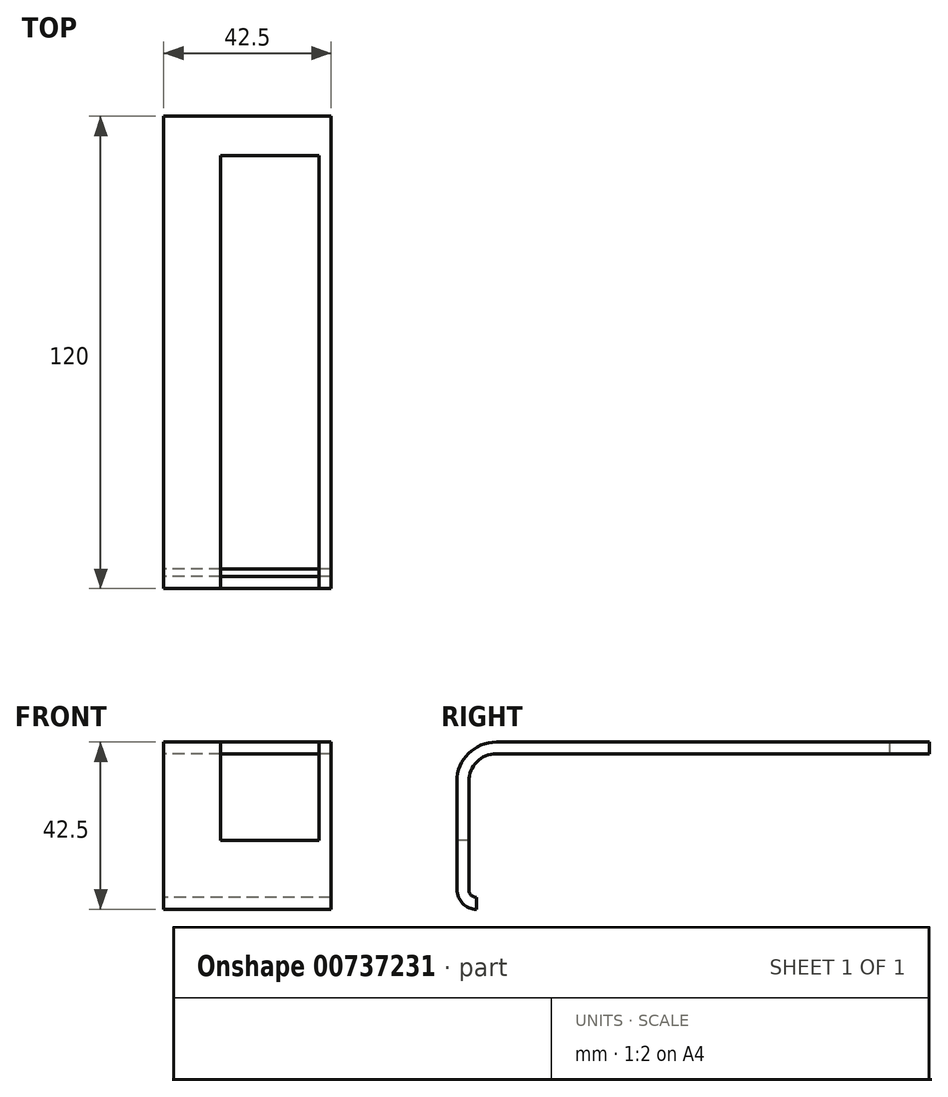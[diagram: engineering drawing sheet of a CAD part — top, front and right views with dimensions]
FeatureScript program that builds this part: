
annotation { "Feature Type Name" : "Feature", "Feature Type Description" : "" }
export const myFeature = defineFeature(function(context is Context, id is Id, definition is map)
    precondition{}
    {
        {
            var Q0;
            Q0=qCreatedBy(makeId("Right.planeOp"),FACE);
            var sketch = newSketch(context, id + "F0", { "sketchPlane" : qUnion([Q0])});
            skLineSegment(sketch, "E0", {"start": v(120, 0) * mm, "end": v(10, 0) * mm});
            skLineSegment(sketch, "E1", {"start": v(0, -10) * mm, "end": v(0, -37.5) * mm});
            skPoint(sketch, "E2.visualSharp", {"position": v(0, 0) * mm});
            skArc(sketch, "E2.filletArc", {"start": v(10, 0) * mm, "mid": v(2.93, -2.93) * mm, "end": v(0, -10) * mm});
            skPoint(sketch, "E3.visualSharp", {"position": v(0, -43) * mm});
            skArc(sketch, "E3.filletArc", {"start": v(0, -37.5) * mm, "mid": v(1.46, -41.04) * mm, "end": v(5, -42.5) * mm});
            skArc(sketch, "E4.0", {"start": v(3, -37.5) * mm, "mid": v(3.59, -38.91) * mm, "end": v(5, -39.5) * mm});
            skLineSegment(sketch, "E5.0", {"start": v(3, -10) * mm, "end": v(3, -37.5) * mm});
            skArc(sketch, "E6.0", {"start": v(10, -3) * mm, "mid": v(5.05, -5.05) * mm, "end": v(3, -10) * mm});
            skLineSegment(sketch, "E7.0", {"start": v(120, -3) * mm, "end": v(10, -3) * mm});
            skLineSegment(sketch, "E8", {"start": v(120, 0) * mm, "end": v(120, -3) * mm});
            skLineSegment(sketch, "E9", {"start": v(5, -39.5) * mm, "end": v(5, -42.5) * mm});
            skSolve(sketch);
        }
        {
            var Q0;
            Q0=qSketchRegion(id+"F0",true);
            extrude(context, id + "F1", {"entities" : qUnion([Q0]), "depth" : 42.5 * mm, "offsetDistance" : 25 * mm});
        }
        {
            var Q0;
            Q0=makeQuery(id+"F1.opExtrude","SWEPT_FACE",FACE,{"disambiguationData":[OSD([sQuery(id+"F0.wireOp",EDGE,"E1")])]});
            var sketch = newSketch(context, id + "F2", { "sketchPlane" : qUnion([Q0])});
            skLineSegment(sketch, "E10.bottom", {"start": v(14.5, -25) * mm, "end": v(39.5, -25) * mm});
            skLineSegment(sketch, "E10.top", {"start": v(14.5, 0) * mm, "end": v(39.5, 0) * mm});
            skLineSegment(sketch, "E10.left", {"start": v(14.5, -25) * mm, "end": v(14.5, 0) * mm});
            skLineSegment(sketch, "E10.right", {"start": v(39.5, -25) * mm, "end": v(39.5, 0) * mm});
            skSolve(sketch);
        }
        {
            var Q0;
            Q0=qSketchRegion(id+"F2",true);
            extrude(context, id + "F3", {"entities" : qUnion([Q0]), "operationType" : NewBodyOperationType.REMOVE, "oppositeDirection" : true, "depth" : 110 * mm, "offsetDistance" : 25 * mm});
        }
    });
